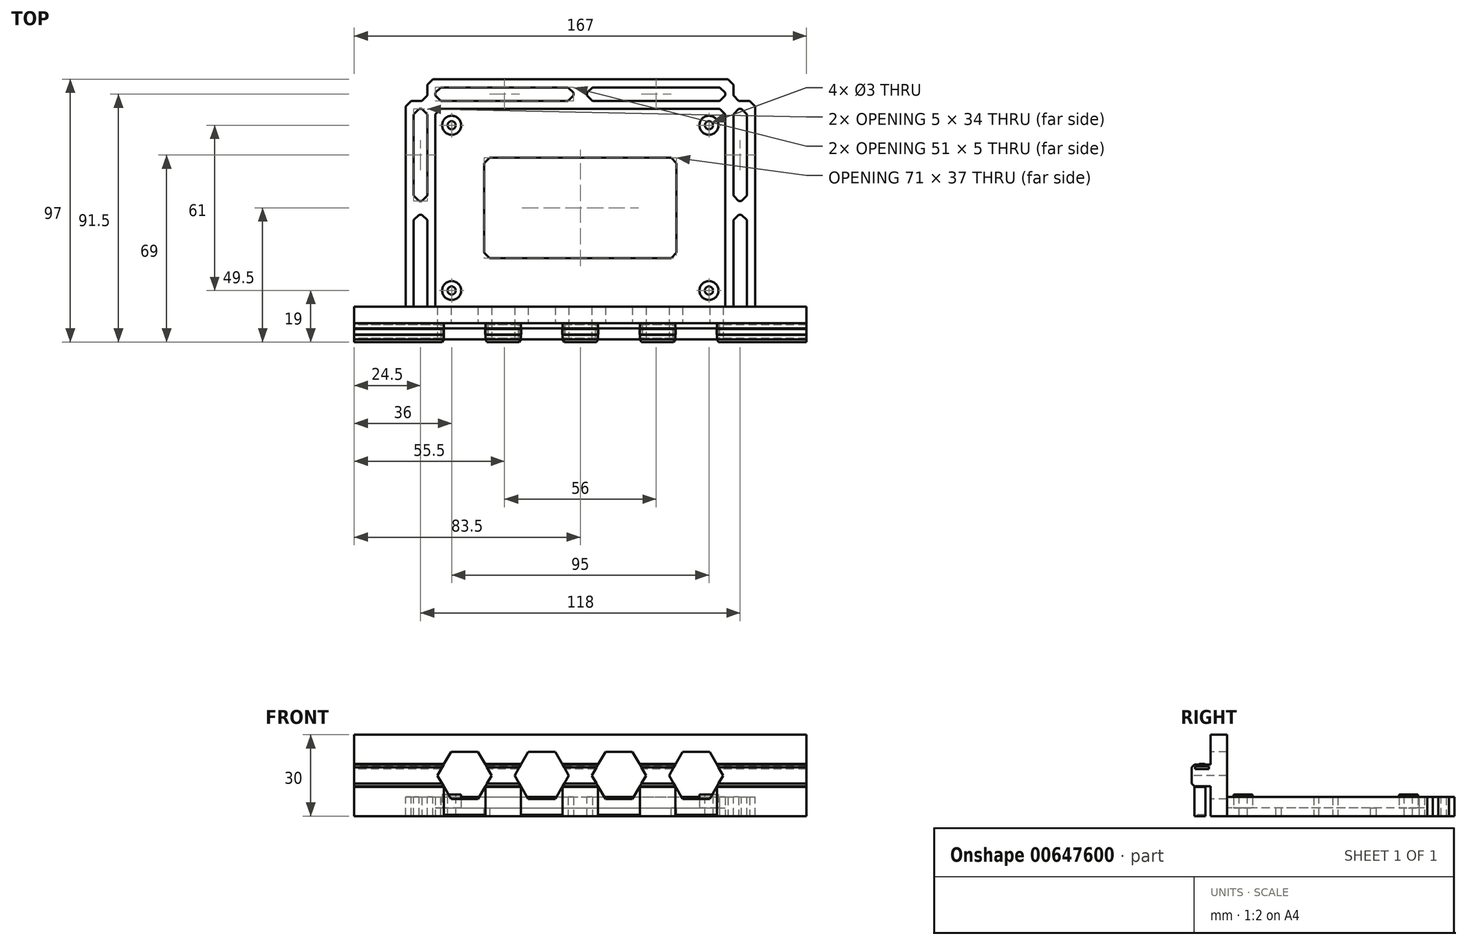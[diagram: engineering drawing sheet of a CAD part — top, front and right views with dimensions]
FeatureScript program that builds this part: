
annotation { "Feature Type Name" : "Feature", "Feature Type Description" : "" }
export const myFeature = defineFeature(function(context is Context, id is Id, definition is map)
    precondition{}
    {
        {
            var Q0;
            Q0=qCreatedBy(makeId("Top.planeOp"),FACE);
            var sketch = newSketch(context, id + "F0", { "sketchPlane" : qUnion([Q0])});
            skLineSegment(sketch, "E0.bottom", {"start": v(-47.5, 30.5) * mm, "end": v(47.5, 30.5) * mm, "construction": true});
            skLineSegment(sketch, "E0.top", {"start": v(-47.5, -30.5) * mm, "end": v(47.5, -30.5) * mm, "construction": true});
            skLineSegment(sketch, "E0.left", {"start": v(-47.5, 30.5) * mm, "end": v(-47.5, -30.5) * mm, "construction": true});
            skLineSegment(sketch, "E0.right", {"start": v(47.5, 30.5) * mm, "end": v(47.5, -30.5) * mm, "construction": true});
            skPoint(sketch, "E0.middle", {"position": v(0, 0) * mm});
            skCircle(sketch, "E1", {"center": v(-47.5, 30.5) * mm, "radius": 1.5 * mm});
            skCircle(sketch, "E2", {"center": v(47.5, 30.5) * mm, "radius": 1.5 * mm});
            skCircle(sketch, "E3", {"center": v(47.5, -30.5) * mm, "radius": 1.5 * mm});
            skCircle(sketch, "E4", {"center": v(-47.5, -30.5) * mm, "radius": 1.5 * mm});
            skCircle(sketch, "E5", {"center": v(-47.5, 30.5) * mm, "radius": 3.5 * mm});
            skCircle(sketch, "E6", {"center": v(47.5, 30.5) * mm, "radius": 3.5 * mm});
            skCircle(sketch, "E7", {"center": v(47.5, -30.5) * mm, "radius": 3.5 * mm});
            skCircle(sketch, "E8", {"center": v(-47.5, -30.5) * mm, "radius": 3.5 * mm});
            skLineSegment(sketch, "E9.0", {"start": v(-53.5, 44.5) * mm, "end": v(-53.5, -36.5) * mm});
            skLineSegment(sketch, "E9.1", {"start": v(-61.5, 36.5) * mm, "end": v(61.5, 36.5) * mm});
            skLineSegment(sketch, "E9.2", {"start": v(53.5, 44.5) * mm, "end": v(53.5, -36.5) * mm});
            skLineSegment(sketch, "E9.3", {"start": v(-83.5, -36.5) * mm, "end": v(83.5, -36.5) * mm});
            skLineSegment(sketch, "E10.0", {"start": v(-56.5, 47.5) * mm, "end": v(-56.5, -36.5) * mm});
            skLineSegment(sketch, "E10.1", {"start": v(-64.5, 39.5) * mm, "end": v(64.5, 39.5) * mm});
            skLineSegment(sketch, "E10.2", {"start": v(56.5, 47.5) * mm, "end": v(56.5, -36.5) * mm});
            skLineSegment(sketch, "E11.0", {"start": v(-61.5, 36.5) * mm, "end": v(-61.5, -36.5) * mm});
            skLineSegment(sketch, "E11.1", {"start": v(-53.5, 44.5) * mm, "end": v(53.5, 44.5) * mm});
            skLineSegment(sketch, "E11.2", {"start": v(61.5, 36.5) * mm, "end": v(61.5, -36.5) * mm});
            skLineSegment(sketch, "E12.0", {"start": v(-64.5, 39.5) * mm, "end": v(-64.5, -36.5) * mm});
            skLineSegment(sketch, "E12.1", {"start": v(-56.5, 47.5) * mm, "end": v(56.5, 47.5) * mm});
            skLineSegment(sketch, "E12.2", {"start": v(64.5, 39.5) * mm, "end": v(64.5, -36.5) * mm});
            skLineSegment(sketch, "E13.0", {"start": v(-35.5, 18.5) * mm, "end": v(-35.5, -18.5) * mm});
            skLineSegment(sketch, "E13.1", {"start": v(-35.5, 18.5) * mm, "end": v(35.5, 18.5) * mm});
            skLineSegment(sketch, "E13.2", {"start": v(35.5, 18.5) * mm, "end": v(35.5, -18.5) * mm});
            skLineSegment(sketch, "E13.3", {"start": v(-35.5, -18.5) * mm, "end": v(35.5, -18.5) * mm});
            skLineSegment(sketch, "E14", {"start": v(-83.5, -36.5) * mm, "end": v(-83.5, -42.5) * mm});
            skLineSegment(sketch, "E15", {"start": v(-83.5, -42.5) * mm, "end": v(83.5, -42.5) * mm});
            skLineSegment(sketch, "E16", {"start": v(83.5, -42.5) * mm, "end": v(83.5, -36.5) * mm});
            skPoint(sketch, "E17", {"position": v(0, -42.5) * mm});
            skLineSegment(sketch, "E18", {"start": v(-61.5, 2.5) * mm, "end": v(-56.5, 2.5) * mm});
            skLineSegment(sketch, "E19", {"start": v(-56.5, -2.5) * mm, "end": v(-61.5, -2.5) * mm});
            skLineSegment(sketch, "E20", {"start": v(-2.5, 44.5) * mm, "end": v(-2.5, 39.5) * mm});
            skLineSegment(sketch, "E21", {"start": v(2.5, 39.5) * mm, "end": v(2.5, 44.5) * mm});
            skLineSegment(sketch, "E22", {"start": v(56.5, 2.5) * mm, "end": v(61.5, 2.5) * mm});
            skLineSegment(sketch, "E23", {"start": v(61.5, -2.5) * mm, "end": v(56.5, -2.5) * mm});
            skPoint(sketch, "E24", {"position": v(0, 44.5) * mm});
            skPoint(sketch, "E25", {"position": v(-61.5, 0) * mm});
            skLineSegment(sketch, "E26", {"start": v(-61.5, 2.5) * mm, "end": v(-61.5, -2.5) * mm, "construction": true});
            skLineSegment(sketch, "E27", {"start": v(-2.5, 44.5) * mm, "end": v(2.5, 44.5) * mm, "construction": true});
            skSolve(sketch);
        }
        {
            var Q0;
            Q0=makeQuery(id+"F0.imprint","IMPRINT",FACE,{"disambiguationData":[TD([[makeQuery(id+"F0.imprint","IMPRINT",EDGE,{"derivedFrom":sQuery(id+"F0.wireOp",EDGE,"E5")}),-1.0]])]});
            var Q1;
            Q1=makeQuery(id+"F0.imprint","IMPRINT",FACE,{"disambiguationData":[TD([[makeQuery(id+"F0.imprint","IMPRINT",EDGE,{"derivedFrom":sQuery(id+"F0.wireOp",EDGE,"E1")}),-1.0]])]});
            var Q2;
            Q2=makeQuery(id+"F0.imprint","IMPRINT",FACE,{"disambiguationData":[TD([[makeQuery(id+"F0.imprint","IMPRINT",EDGE,{"derivedFrom":sQuery(id+"F0.wireOp",EDGE,"E4")}),-1.0]])]});
            var Q3;
            Q3=makeQuery(id+"F0.imprint","IMPRINT",FACE,{"disambiguationData":[TD([[makeQuery(id+"F0.imprint","IMPRINT",EDGE,{"derivedFrom":sQuery(id+"F0.wireOp",EDGE,"E3")}),-1.0]])]});
            var Q4;
            Q4=makeQuery(id+"F0.imprint","IMPRINT",FACE,{"disambiguationData":[TD([[makeQuery(id+"F0.imprint","IMPRINT",EDGE,{"derivedFrom":sQuery(id+"F0.wireOp",EDGE,"E2")}),-1.0]])]});
            var Q5;
            {var subQ0=sQuery(id+"F0.wireOp",EDGE,"E9.3");var subQ1=sQuery(id+"F0.wireOp",EDGE,"E9.0");var subQ2=makeQuery(id+"F0.imprint","INTERSECT",VERTEX,{"derivedFrom":[subQ1,subQ0]});Q5=makeQuery(id+"F0.imprint","IMPRINT",FACE,{"disambiguationData":[TD([[makeQuery(id+"F0.imprint","IMPRINT",EDGE,{"disambiguationData":[TD([[subQ2,1.0]])],"derivedFrom":subQ1}),-1.0]])]});}
            var Q6;
            {var subQ0=sQuery(id+"F0.wireOp",EDGE,"E12.0");Q6=makeQuery(id+"F0.imprint","IMPRINT",FACE,{"disambiguationData":[TD([[makeQuery(id+"F0.imprint","IMPRINT",EDGE,{"derivedFrom":subQ0}),1.0]])]});}
            var Q7;
            {var subQ0=sQuery(id+"F0.wireOp",EDGE,"E18");Q7=makeQuery(id+"F0.imprint","IMPRINT",FACE,{"disambiguationData":[TD([[makeQuery(id+"F0.imprint","IMPRINT",EDGE,{"derivedFrom":subQ0}),-1.0]])]});}
            var Q8;
            {var subQ0=sQuery(id+"F0.wireOp",EDGE,"E10.1");var subQ1=sQuery(id+"F0.wireOp",EDGE,"E9.0");var subQ2=makeQuery(id+"F0.imprint","INTERSECT",VERTEX,{"derivedFrom":[subQ1,subQ0]});Q8=makeQuery(id+"F0.imprint","IMPRINT",FACE,{"disambiguationData":[TD([[makeQuery(id+"F0.imprint","IMPRINT",EDGE,{"disambiguationData":[TD([[subQ2,-1.0]])],"derivedFrom":subQ1}),-1.0]])]});}
            var Q9;
            {var subQ13=sQuery(id+"F0.wireOp",EDGE,"E12.1");Q9=makeQuery(id+"F0.imprint","IMPRINT",FACE,{"disambiguationData":[TD([[makeQuery(id+"F0.imprint","IMPRINT",EDGE,{"derivedFrom":subQ13}),-1.0]])]});}
            var Q10;
            {var subQ0=sQuery(id+"F0.wireOp",EDGE,"E10.1");var subQ2=sQuery(id+"F0.wireOp",EDGE,"E9.0");var subQ3=makeQuery(id+"F0.imprint","INTERSECT",VERTEX,{"derivedFrom":[subQ2,subQ0]});Q10=makeQuery(id+"F0.imprint","IMPRINT",FACE,{"disambiguationData":[TD([[makeQuery(id+"F0.imprint","IMPRINT",EDGE,{"disambiguationData":[TD([[subQ3,-1.0]])],"derivedFrom":subQ2}),1.0]])]});}
            var Q11;
            {var subQ0=sQuery(id+"F0.wireOp",EDGE,"E14");Q11=makeQuery(id+"F0.imprint","IMPRINT",FACE,{"disambiguationData":[TD([[makeQuery(id+"F0.imprint","IMPRINT",EDGE,{"derivedFrom":subQ0}),1.0]])]});}
            var Q12;
            {var subQ0=sQuery(id+"F0.wireOp",EDGE,"E20");Q12=makeQuery(id+"F0.imprint","IMPRINT",FACE,{"disambiguationData":[TD([[makeQuery(id+"F0.imprint","IMPRINT",EDGE,{"derivedFrom":subQ0}),1.0]])]});}
            var Q13;
            {var subQ0=sQuery(id+"F0.wireOp",EDGE,"E9.2");var subQ1=sQuery(id+"F0.wireOp",EDGE,"E9.1");var subQ2=makeQuery(id+"F0.imprint","INTERSECT",VERTEX,{"derivedFrom":[subQ1,subQ0]});Q13=makeQuery(id+"F0.imprint","IMPRINT",FACE,{"disambiguationData":[TD([[makeQuery(id+"F0.imprint","IMPRINT",EDGE,{"disambiguationData":[TD([[subQ2,-1.0]])],"derivedFrom":subQ1}),1.0]])]});}
            var Q14;
            {var subQ0=sQuery(id+"F0.wireOp",EDGE,"E12.2");Q14=makeQuery(id+"F0.imprint","IMPRINT",FACE,{"disambiguationData":[TD([[makeQuery(id+"F0.imprint","IMPRINT",EDGE,{"derivedFrom":subQ0}),-1.0]])]});}
            var Q15;
            {var subQ0=sQuery(id+"F0.wireOp",EDGE,"E22");Q15=makeQuery(id+"F0.imprint","IMPRINT",FACE,{"disambiguationData":[TD([[makeQuery(id+"F0.imprint","IMPRINT",EDGE,{"derivedFrom":subQ0}),-1.0]])]});}
            var Q16;
            {var subQ2=sQuery(id+"F0.wireOp",EDGE,"E9.1");var subQ5=sQuery(id+"F0.wireOp",EDGE,"E9.2");var subQ7=makeQuery(id+"F0.imprint","INTERSECT",VERTEX,{"derivedFrom":[subQ2,subQ5]});Q16=makeQuery(id+"F0.imprint","IMPRINT",FACE,{"disambiguationData":[TD([[makeQuery(id+"F0.imprint","IMPRINT",EDGE,{"disambiguationData":[TD([[subQ7,-1.0]])],"derivedFrom":subQ2}),-1.0]])]});}
            extrude(context, id + "F1", {"entities" : qUnion([Q0, Q1, Q2, Q3, Q4, Q5, Q6, Q7, Q8, Q9, Q10, Q11, Q12, Q13, Q14, Q15, Q16]), "oppositeDirection" : true, "depth" : 3 * mm, "offsetDistance" : 25 * mm});
        }
        {
            var Q0;
            {var subQ0=sQuery(id+"F0.wireOp",EDGE,"E9.3");var subQ1=sQuery(id+"F0.wireOp",EDGE,"E9.0");var subQ2=makeQuery(id+"F0.imprint","INTERSECT",VERTEX,{"derivedFrom":[subQ1,subQ0]});Q0=makeQuery(id+"F0.imprint","IMPRINT",FACE,{"disambiguationData":[TD([[makeQuery(id+"F0.imprint","IMPRINT",EDGE,{"disambiguationData":[TD([[subQ2,1.0]])],"derivedFrom":subQ1}),-1.0]])]});}
            var Q1;
            {var subQ0=sQuery(id+"F0.wireOp",EDGE,"E10.1");var subQ1=sQuery(id+"F0.wireOp",EDGE,"E9.0");var subQ2=makeQuery(id+"F0.imprint","INTERSECT",VERTEX,{"derivedFrom":[subQ1,subQ0]});Q1=makeQuery(id+"F0.imprint","IMPRINT",FACE,{"disambiguationData":[TD([[makeQuery(id+"F0.imprint","IMPRINT",EDGE,{"disambiguationData":[TD([[subQ2,-1.0]])],"derivedFrom":subQ1}),-1.0]])]});}
            var Q2;
            {var subQ13=sQuery(id+"F0.wireOp",EDGE,"E12.1");Q2=makeQuery(id+"F0.imprint","IMPRINT",FACE,{"disambiguationData":[TD([[makeQuery(id+"F0.imprint","IMPRINT",EDGE,{"derivedFrom":subQ13}),-1.0]])]});}
            var Q3;
            {var subQ0=sQuery(id+"F0.wireOp",EDGE,"E12.0");Q3=makeQuery(id+"F0.imprint","IMPRINT",FACE,{"disambiguationData":[TD([[makeQuery(id+"F0.imprint","IMPRINT",EDGE,{"derivedFrom":subQ0}),1.0]])]});}
            var Q4;
            {var subQ0=sQuery(id+"F0.wireOp",EDGE,"E18");Q4=makeQuery(id+"F0.imprint","IMPRINT",FACE,{"disambiguationData":[TD([[makeQuery(id+"F0.imprint","IMPRINT",EDGE,{"derivedFrom":subQ0}),-1.0]])]});}
            var Q5;
            {var subQ0=sQuery(id+"F0.wireOp",EDGE,"E20");Q5=makeQuery(id+"F0.imprint","IMPRINT",FACE,{"disambiguationData":[TD([[makeQuery(id+"F0.imprint","IMPRINT",EDGE,{"derivedFrom":subQ0}),1.0]])]});}
            var Q6;
            {var subQ0=sQuery(id+"F0.wireOp",EDGE,"E10.1");var subQ2=sQuery(id+"F0.wireOp",EDGE,"E9.0");var subQ3=makeQuery(id+"F0.imprint","INTERSECT",VERTEX,{"derivedFrom":[subQ2,subQ0]});Q6=makeQuery(id+"F0.imprint","IMPRINT",FACE,{"disambiguationData":[TD([[makeQuery(id+"F0.imprint","IMPRINT",EDGE,{"disambiguationData":[TD([[subQ3,-1.0]])],"derivedFrom":subQ2}),1.0]])]});}
            var Q7;
            {var subQ0=sQuery(id+"F0.wireOp",EDGE,"E9.2");var subQ1=sQuery(id+"F0.wireOp",EDGE,"E9.1");var subQ2=makeQuery(id+"F0.imprint","INTERSECT",VERTEX,{"derivedFrom":[subQ1,subQ0]});Q7=makeQuery(id+"F0.imprint","IMPRINT",FACE,{"disambiguationData":[TD([[makeQuery(id+"F0.imprint","IMPRINT",EDGE,{"disambiguationData":[TD([[subQ2,-1.0]])],"derivedFrom":subQ1}),1.0]])]});}
            var Q8;
            {var subQ2=sQuery(id+"F0.wireOp",EDGE,"E9.1");var subQ5=sQuery(id+"F0.wireOp",EDGE,"E9.2");var subQ7=makeQuery(id+"F0.imprint","INTERSECT",VERTEX,{"derivedFrom":[subQ2,subQ5]});Q8=makeQuery(id+"F0.imprint","IMPRINT",FACE,{"disambiguationData":[TD([[makeQuery(id+"F0.imprint","IMPRINT",EDGE,{"disambiguationData":[TD([[subQ7,-1.0]])],"derivedFrom":subQ2}),-1.0]])]});}
            var Q9;
            {var subQ0=sQuery(id+"F0.wireOp",EDGE,"E12.2");Q9=makeQuery(id+"F0.imprint","IMPRINT",FACE,{"disambiguationData":[TD([[makeQuery(id+"F0.imprint","IMPRINT",EDGE,{"derivedFrom":subQ0}),-1.0]])]});}
            var Q10;
            {var subQ0=sQuery(id+"F0.wireOp",EDGE,"E22");Q10=makeQuery(id+"F0.imprint","IMPRINT",FACE,{"disambiguationData":[TD([[makeQuery(id+"F0.imprint","IMPRINT",EDGE,{"derivedFrom":subQ0}),-1.0]])]});}
            extrude(context, id + "F2", {"entities" : qUnion([Q0, Q1, Q2, Q3, Q4, Q5, Q6, Q7, Q8, Q9, Q10]), "operationType" : NewBodyOperationType.ADD, "depth" : 4 * mm, "offsetDistance" : 25 * mm});
        }
        {
            var Q0;
            Q0=makeQuery(id+"F0.imprint","IMPRINT",FACE,{"disambiguationData":[TD([[makeQuery(id+"F0.imprint","IMPRINT",EDGE,{"derivedFrom":sQuery(id+"F0.wireOp",EDGE,"E1")}),-1.0]])]});
            var Q1;
            Q1=makeQuery(id+"F0.imprint","IMPRINT",FACE,{"disambiguationData":[TD([[makeQuery(id+"F0.imprint","IMPRINT",EDGE,{"derivedFrom":sQuery(id+"F0.wireOp",EDGE,"E2")}),-1.0]])]});
            var Q2;
            Q2=makeQuery(id+"F0.imprint","IMPRINT",FACE,{"disambiguationData":[TD([[makeQuery(id+"F0.imprint","IMPRINT",EDGE,{"derivedFrom":sQuery(id+"F0.wireOp",EDGE,"E3")}),-1.0]])]});
            var Q3;
            Q3=makeQuery(id+"F0.imprint","IMPRINT",FACE,{"disambiguationData":[TD([[makeQuery(id+"F0.imprint","IMPRINT",EDGE,{"derivedFrom":sQuery(id+"F0.wireOp",EDGE,"E4")}),-1.0]])]});
            extrude(context, id + "F3", {"entities" : qUnion([Q0, Q1, Q2, Q3]), "operationType" : NewBodyOperationType.ADD, "depth" : 5 * mm, "offsetDistance" : 25 * mm});
        }
        {
            var Q0;
            {var subQ0=sQuery(id+"F0.wireOp",EDGE,"E14");Q0=makeQuery(id+"F0.imprint","IMPRINT",FACE,{"disambiguationData":[TD([[makeQuery(id+"F0.imprint","IMPRINT",EDGE,{"derivedFrom":subQ0}),1.0]])]});}
            extrude(context, id + "F4", {"entities" : qUnion([Q0]), "operationType" : NewBodyOperationType.ADD, "depth" : 27 * mm, "offsetDistance" : 25 * mm});
        }
        {
            var Q0;
            {var subQ0=sQuery(id+"F0.wireOp",EDGE,"E15");Q0=makeQuery(id+"F4.boolean.opBoolean","MERGE",FACE,{"derivedFrom":[makeQuery(id+"F1.opExtrude","SWEPT_FACE",FACE,{"disambiguationData":[OSD([subQ0])]}),makeQuery(id+"F4.opExtrude","SWEPT_FACE",FACE,{"disambiguationData":[OSD([subQ0])]})]});}
            var sketch = newSketch(context, id + "F5", { "sketchPlane" : qUnion([Q0])});
            skLineSegment(sketch, "E28.bottom", {"start": v(-83.5, 16) * mm, "end": v(83.5, 16) * mm});
            skLineSegment(sketch, "E28.top", {"start": v(-83.5, 8) * mm, "end": v(83.5, 8) * mm});
            skLineSegment(sketch, "E28.left", {"start": v(-83.5, 16) * mm, "end": v(-83.5, 8) * mm});
            skLineSegment(sketch, "E28.right", {"start": v(83.5, 16) * mm, "end": v(83.5, 8) * mm});
            skPoint(sketch, "E29", {"position": v(-83.5, 12) * mm});
            skCircle(sketch, "E30", {"center": v(-68.5, 12) * mm, "radius": 3.05 * mm});
            skCircle(sketch, "E31", {"center": v(-68.5, 12) * mm, "radius": 5.6 * mm});
            skCircle(sketch, "E32", {"center": v(68.5, 12) * mm, "radius": 3.05 * mm});
            skCircle(sketch, "E33", {"center": v(68.5, 12) * mm, "radius": 5.6 * mm});
            skCircle(sketch, "E34.cCircle", {"center": v(-42.75, 12) * mm, "radius": 10 * mm, "construction": true});
            skLineSegment(sketch, "E34.0", {"start": v(-32.75, 12) * mm, "end": v(-37.75, 3.34) * mm});
            skLineSegment(sketch, "E34.1", {"start": v(-37.75, 3.34) * mm, "end": v(-47.75, 3.34) * mm});
            skLineSegment(sketch, "E34.2", {"start": v(-47.75, 3.34) * mm, "end": v(-52.75, 12) * mm});
            skLineSegment(sketch, "E34.3", {"start": v(-52.75, 12) * mm, "end": v(-47.75, 20.66) * mm});
            skLineSegment(sketch, "E34.4", {"start": v(-47.75, 20.66) * mm, "end": v(-37.75, 20.66) * mm});
            skLineSegment(sketch, "E34.5", {"start": v(-37.75, 20.66) * mm, "end": v(-32.75, 12) * mm});
            skCircle(sketch, "E35.cCircle", {"center": v(-14.25, 12) * mm, "radius": 10 * mm, "construction": true});
            skLineSegment(sketch, "E35.0", {"start": v(-4.25, 12) * mm, "end": v(-9.25, 3.34) * mm});
            skLineSegment(sketch, "E35.1", {"start": v(-9.25, 3.34) * mm, "end": v(-19.25, 3.34) * mm});
            skLineSegment(sketch, "E35.2", {"start": v(-19.25, 3.34) * mm, "end": v(-24.25, 12) * mm});
            skLineSegment(sketch, "E35.3", {"start": v(-24.25, 12) * mm, "end": v(-19.25, 20.66) * mm});
            skLineSegment(sketch, "E35.4", {"start": v(-19.25, 20.66) * mm, "end": v(-9.25, 20.66) * mm});
            skLineSegment(sketch, "E35.5", {"start": v(-9.25, 20.66) * mm, "end": v(-4.25, 12) * mm});
            skCircle(sketch, "E36.cCircle", {"center": v(14.25, 12) * mm, "radius": 10 * mm, "construction": true});
            skLineSegment(sketch, "E36.0", {"start": v(24.25, 12) * mm, "end": v(19.25, 3.34) * mm});
            skLineSegment(sketch, "E36.1", {"start": v(19.25, 3.34) * mm, "end": v(9.25, 3.34) * mm});
            skLineSegment(sketch, "E36.2", {"start": v(9.25, 3.34) * mm, "end": v(4.25, 12) * mm});
            skLineSegment(sketch, "E36.3", {"start": v(4.25, 12) * mm, "end": v(9.25, 20.66) * mm});
            skLineSegment(sketch, "E36.4", {"start": v(9.25, 20.66) * mm, "end": v(19.25, 20.66) * mm});
            skLineSegment(sketch, "E36.5", {"start": v(19.25, 20.66) * mm, "end": v(24.25, 12) * mm});
            skCircle(sketch, "E37.cCircle", {"center": v(42.75, 12) * mm, "radius": 10 * mm, "construction": true});
            skLineSegment(sketch, "E37.0", {"start": v(52.75, 12) * mm, "end": v(47.75, 3.34) * mm});
            skLineSegment(sketch, "E37.1", {"start": v(47.75, 3.34) * mm, "end": v(37.75, 3.34) * mm});
            skLineSegment(sketch, "E37.2", {"start": v(37.75, 3.34) * mm, "end": v(32.75, 12) * mm});
            skLineSegment(sketch, "E37.3", {"start": v(32.75, 12) * mm, "end": v(37.75, 20.66) * mm});
            skLineSegment(sketch, "E37.4", {"start": v(37.75, 20.66) * mm, "end": v(47.75, 20.66) * mm});
            skLineSegment(sketch, "E37.5", {"start": v(47.75, 20.66) * mm, "end": v(52.75, 12) * mm});
            skLineSegment(sketch, "E38", {"start": v(-32.75, 12) * mm, "end": v(-24.25, 12) * mm, "construction": true});
            skLineSegment(sketch, "E39", {"start": v(-4.25, 12) * mm, "end": v(4.25, 12) * mm, "construction": true});
            skLineSegment(sketch, "E40", {"start": v(24.25, 12) * mm, "end": v(32.75, 12) * mm, "construction": true});
            skLineSegment(sketch, "E41", {"start": v(-68.5, 12) * mm, "end": v(-52.75, 12) * mm, "construction": true});
            skLineSegment(sketch, "E42", {"start": v(52.75, 12) * mm, "end": v(68.5, 12) * mm, "construction": true});
            skLineSegment(sketch, "E43", {"start": v(-83.5, 12) * mm, "end": v(-68.5, 12) * mm, "construction": true});
            skLineSegment(sketch, "E44", {"start": v(68.5, 12) * mm, "end": v(83.5, 12) * mm, "construction": true});
            skLineSegment(sketch, "E45", {"start": v(-76, 16) * mm, "end": v(-76, 8) * mm});
            skLineSegment(sketch, "E46", {"start": v(-61, 8) * mm, "end": v(-61, 16) * mm});
            skLineSegment(sketch, "E47", {"start": v(76, 16) * mm, "end": v(76, 8) * mm});
            skLineSegment(sketch, "E48", {"start": v(61, 8) * mm, "end": v(61, 16) * mm});
            skLineSegment(sketch, "E49", {"start": v(-76, 12) * mm, "end": v(-61, 12) * mm, "construction": true});
            skLineSegment(sketch, "E50", {"start": v(61, 12) * mm, "end": v(76, 12) * mm, "construction": true});
            skPoint(sketch, "E50.endSnap0", {"position": v(76, 12) * mm});
            skSolve(sketch);
        }
        {
            var Q0;
            {var subQ5=sQuery(id+"F5.wireOp",EDGE,"E34.4");Q0=makeQuery(id+"F5.imprint","IMPRINT",FACE,{"disambiguationData":[TD([[makeQuery(id+"F5.imprint","IMPRINT",EDGE,{"derivedFrom":subQ5}),-1.0]])]});}
            var Q1;
            {var subQ7=sQuery(id+"F5.wireOp",EDGE,"E28.bottom");var subQ9=sQuery(id+"F5.wireOp",EDGE,"E34.3");var subQ11=makeQuery(id+"F5.imprint","INTERSECT",VERTEX,{"derivedFrom":[subQ7,subQ9]});Q1=makeQuery(id+"F5.imprint","IMPRINT",FACE,{"disambiguationData":[TD([[makeQuery(id+"F5.imprint","IMPRINT",EDGE,{"disambiguationData":[TD([[subQ11,-1.0]])],"derivedFrom":subQ7}),-1.0]])]});}
            var Q2;
            {var subQ5=sQuery(id+"F5.wireOp",EDGE,"E34.1");Q2=makeQuery(id+"F5.imprint","IMPRINT",FACE,{"disambiguationData":[TD([[makeQuery(id+"F5.imprint","IMPRINT",EDGE,{"derivedFrom":subQ5}),-1.0]])]});}
            var Q3;
            {var subQ5=sQuery(id+"F5.wireOp",EDGE,"E35.1");Q3=makeQuery(id+"F5.imprint","IMPRINT",FACE,{"disambiguationData":[TD([[makeQuery(id+"F5.imprint","IMPRINT",EDGE,{"derivedFrom":subQ5}),-1.0]])]});}
            var Q4;
            {var subQ0=sQuery(id+"F5.wireOp",EDGE,"E35.3");var subQ9=sQuery(id+"F5.wireOp",EDGE,"E28.bottom");var subQ10=makeQuery(id+"F5.imprint","INTERSECT",VERTEX,{"derivedFrom":[subQ9,subQ0]});Q4=makeQuery(id+"F5.imprint","IMPRINT",FACE,{"disambiguationData":[TD([[makeQuery(id+"F5.imprint","IMPRINT",EDGE,{"disambiguationData":[TD([[subQ10,-1.0]])],"derivedFrom":subQ9}),-1.0]])]});}
            var Q5;
            {var subQ5=sQuery(id+"F5.wireOp",EDGE,"E35.4");Q5=makeQuery(id+"F5.imprint","IMPRINT",FACE,{"disambiguationData":[TD([[makeQuery(id+"F5.imprint","IMPRINT",EDGE,{"derivedFrom":subQ5}),-1.0]])]});}
            var Q6;
            {var subQ5=sQuery(id+"F5.wireOp",EDGE,"E36.4");Q6=makeQuery(id+"F5.imprint","IMPRINT",FACE,{"disambiguationData":[TD([[makeQuery(id+"F5.imprint","IMPRINT",EDGE,{"derivedFrom":subQ5}),-1.0]])]});}
            var Q7;
            {var subQ0=sQuery(id+"F5.wireOp",EDGE,"E36.3");var subQ9=sQuery(id+"F5.wireOp",EDGE,"E28.bottom");var subQ10=makeQuery(id+"F5.imprint","INTERSECT",VERTEX,{"derivedFrom":[subQ9,subQ0]});Q7=makeQuery(id+"F5.imprint","IMPRINT",FACE,{"disambiguationData":[TD([[makeQuery(id+"F5.imprint","IMPRINT",EDGE,{"disambiguationData":[TD([[subQ10,-1.0]])],"derivedFrom":subQ9}),-1.0]])]});}
            var Q8;
            {var subQ5=sQuery(id+"F5.wireOp",EDGE,"E36.1");Q8=makeQuery(id+"F5.imprint","IMPRINT",FACE,{"disambiguationData":[TD([[makeQuery(id+"F5.imprint","IMPRINT",EDGE,{"derivedFrom":subQ5}),-1.0]])]});}
            var Q9;
            {var subQ5=sQuery(id+"F5.wireOp",EDGE,"E37.1");Q9=makeQuery(id+"F5.imprint","IMPRINT",FACE,{"disambiguationData":[TD([[makeQuery(id+"F5.imprint","IMPRINT",EDGE,{"derivedFrom":subQ5}),-1.0]])]});}
            var Q10;
            {var subQ0=sQuery(id+"F5.wireOp",EDGE,"E37.3");var subQ9=sQuery(id+"F5.wireOp",EDGE,"E28.bottom");var subQ10=makeQuery(id+"F5.imprint","INTERSECT",VERTEX,{"derivedFrom":[subQ9,subQ0]});Q10=makeQuery(id+"F5.imprint","IMPRINT",FACE,{"disambiguationData":[TD([[makeQuery(id+"F5.imprint","IMPRINT",EDGE,{"disambiguationData":[TD([[subQ10,-1.0]])],"derivedFrom":subQ9}),-1.0]])]});}
            var Q11;
            {var subQ5=sQuery(id+"F5.wireOp",EDGE,"E37.4");Q11=makeQuery(id+"F5.imprint","IMPRINT",FACE,{"disambiguationData":[TD([[makeQuery(id+"F5.imprint","IMPRINT",EDGE,{"derivedFrom":subQ5}),-1.0]])]});}
            var Q12;
            {var subQ0=sQuery(id+"F0.wireOp",EDGE,"E9.3");Q12=makeQuery(id+"F4.boolean.opBoolean","MERGE",FACE,{"derivedFrom":[makeQuery(id+"F1.opExtrude","SWEPT_FACE",FACE,{"disambiguationData":[OSD([subQ0]),TDD([makeQuery(id+"F0.imprint","IMPRINT",EDGE,{"disambiguationData":[TD([[makeQuery(id+"F0.imprint","INTERSECT",VERTEX,{"derivedFrom":[subQ0,sQuery(id+"F0.wireOp",EDGE,"E14")]}),-1.0]])],"derivedFrom":subQ0})])]}),makeQuery(id+"F1.opExtrude","SWEPT_FACE",FACE,{"disambiguationData":[OSD([subQ0]),TDD([makeQuery(id+"F0.imprint","IMPRINT",EDGE,{"disambiguationData":[TD([[makeQuery(id+"F0.imprint","INTERSECT",VERTEX,{"derivedFrom":[subQ0,sQuery(id+"F0.wireOp",EDGE,"E10.0")]}),1.0]])],"derivedFrom":subQ0})])]}),makeQuery(id+"F1.opExtrude","SWEPT_FACE",FACE,{"disambiguationData":[OSD([subQ0]),TDD([makeQuery(id+"F0.imprint","IMPRINT",EDGE,{"disambiguationData":[TD([[makeQuery(id+"F0.imprint","INTERSECT",VERTEX,{"derivedFrom":[subQ0,sQuery(id+"F0.wireOp",EDGE,"E10.2")]}),-1.0]])],"derivedFrom":subQ0})])]}),makeQuery(id+"F1.opExtrude","SWEPT_FACE",FACE,{"disambiguationData":[OSD([subQ0]),TDD([makeQuery(id+"F0.imprint","IMPRINT",EDGE,{"disambiguationData":[TD([[makeQuery(id+"F0.imprint","INTERSECT",VERTEX,{"derivedFrom":[subQ0,sQuery(id+"F0.wireOp",EDGE,"E16")]}),1.0]])],"derivedFrom":subQ0})])]}),makeQuery(id+"F4.opExtrude","SWEPT_FACE",FACE,{"disambiguationData":[OSD([subQ0])]})]});}
            extrude(context, id + "F6", {"entities" : qUnion([Q0, Q1, Q2, Q3, Q4, Q5, Q6, Q7, Q8, Q9, Q10, Q11]), "operationType" : NewBodyOperationType.REMOVE, "endBound" : BoundingType.UP_TO_SURFACE, "oppositeDirection" : true, "depth" : 25 * mm, "endBoundEntityFace" : qUnion([Q12]), "offsetDistance" : 25 * mm});
        }
        {
            var Q0;
            {var subQ0=sQuery(id+"F5.wireOp",EDGE,"E28.left");Q0=makeQuery(id+"F5.imprint","IMPRINT",FACE,{"disambiguationData":[TD([[makeQuery(id+"F5.imprint","IMPRINT",EDGE,{"derivedFrom":subQ0}),-1.0]])]});}
            var Q1;
            {var subQ0=sQuery(id+"F5.wireOp",EDGE,"E28.right");Q1=makeQuery(id+"F5.imprint","IMPRINT",FACE,{"disambiguationData":[TD([[makeQuery(id+"F5.imprint","IMPRINT",EDGE,{"derivedFrom":subQ0}),1.0]])]});}
            var Q2;
            {var subQ7=sQuery(id+"F5.wireOp",EDGE,"E48");Q2=makeQuery(id+"F5.imprint","IMPRINT",FACE,{"disambiguationData":[TD([[makeQuery(id+"F5.imprint","IMPRINT",EDGE,{"derivedFrom":subQ7}),1.0]])]});}
            var Q3;
            {var subQ0=sQuery(id+"F5.wireOp",EDGE,"E36.5");var subQ7=sQuery(id+"F5.wireOp",EDGE,"E28.bottom");var subQ8=makeQuery(id+"F5.imprint","INTERSECT",VERTEX,{"derivedFrom":[subQ7,subQ0]});Q3=makeQuery(id+"F5.imprint","IMPRINT",FACE,{"disambiguationData":[TD([[makeQuery(id+"F5.imprint","IMPRINT",EDGE,{"disambiguationData":[TD([[subQ8,-1.0]])],"derivedFrom":subQ7}),-1.0]])]});}
            var Q4;
            {var subQ0=sQuery(id+"F5.wireOp",EDGE,"E35.5");var subQ5=sQuery(id+"F5.wireOp",EDGE,"E28.bottom");var subQ6=makeQuery(id+"F5.imprint","INTERSECT",VERTEX,{"derivedFrom":[subQ5,subQ0]});Q4=makeQuery(id+"F5.imprint","IMPRINT",FACE,{"disambiguationData":[TD([[makeQuery(id+"F5.imprint","IMPRINT",EDGE,{"disambiguationData":[TD([[subQ6,-1.0]])],"derivedFrom":subQ5}),-1.0]])]});}
            var Q5;
            {var subQ0=sQuery(id+"F5.wireOp",EDGE,"E34.5");var subQ3=sQuery(id+"F5.wireOp",EDGE,"E28.bottom");var subQ4=makeQuery(id+"F5.imprint","INTERSECT",VERTEX,{"derivedFrom":[subQ3,subQ0]});Q5=makeQuery(id+"F5.imprint","IMPRINT",FACE,{"disambiguationData":[TD([[makeQuery(id+"F5.imprint","IMPRINT",EDGE,{"disambiguationData":[TD([[subQ4,-1.0]])],"derivedFrom":subQ3}),-1.0]])]});}
            var Q6;
            {var subQ7=sQuery(id+"F5.wireOp",EDGE,"E46");Q6=makeQuery(id+"F5.imprint","IMPRINT",FACE,{"disambiguationData":[TD([[makeQuery(id+"F5.imprint","IMPRINT",EDGE,{"derivedFrom":subQ7}),-1.0]])]});}
            var Q7;
            {var subQ0=sQuery(id+"F5.wireOp",EDGE,"E48");Q7=makeQuery(id+"F5.imprint","IMPRINT",FACE,{"disambiguationData":[TD([[makeQuery(id+"F5.imprint","IMPRINT",EDGE,{"derivedFrom":subQ0}),-1.0]])]});}
            var Q8;
            Q8=makeQuery(id+"F5.imprint","IMPRINT",FACE,{"disambiguationData":[TD([[makeQuery(id+"F5.imprint","IMPRINT",EDGE,{"derivedFrom":sQuery(id+"F5.wireOp",EDGE,"E32")}),-1.0]])]});
            var Q9;
            Q9=makeQuery(id+"F5.imprint","IMPRINT",FACE,{"disambiguationData":[TD([[makeQuery(id+"F5.imprint","IMPRINT",EDGE,{"derivedFrom":sQuery(id+"F5.wireOp",EDGE,"E32")}),1.0]])]});
            var Q10;
            {var subQ0=sQuery(id+"F5.wireOp",EDGE,"E47");Q10=makeQuery(id+"F5.imprint","IMPRINT",FACE,{"disambiguationData":[TD([[makeQuery(id+"F5.imprint","IMPRINT",EDGE,{"derivedFrom":subQ0}),-1.0]])]});}
            var Q11;
            {var subQ0=sQuery(id+"F5.wireOp",EDGE,"E46");Q11=makeQuery(id+"F5.imprint","IMPRINT",FACE,{"disambiguationData":[TD([[makeQuery(id+"F5.imprint","IMPRINT",EDGE,{"derivedFrom":subQ0}),1.0]])]});}
            var Q12;
            Q12=makeQuery(id+"F5.imprint","IMPRINT",FACE,{"disambiguationData":[TD([[makeQuery(id+"F5.imprint","IMPRINT",EDGE,{"derivedFrom":sQuery(id+"F5.wireOp",EDGE,"E30")}),-1.0]])]});
            var Q13;
            Q13=makeQuery(id+"F5.imprint","IMPRINT",FACE,{"disambiguationData":[TD([[makeQuery(id+"F5.imprint","IMPRINT",EDGE,{"derivedFrom":sQuery(id+"F5.wireOp",EDGE,"E30")}),1.0]])]});
            var Q14;
            {var subQ0=sQuery(id+"F5.wireOp",EDGE,"E45");Q14=makeQuery(id+"F5.imprint","IMPRINT",FACE,{"disambiguationData":[TD([[makeQuery(id+"F5.imprint","IMPRINT",EDGE,{"derivedFrom":subQ0}),1.0]])]});}
            extrude(context, id + "F7", {"entities" : qUnion([Q0, Q1, Q2, Q3, Q4, Q5, Q6, Q7, Q8, Q9, Q10, Q11, Q12, Q13, Q14]), "operationType" : NewBodyOperationType.ADD, "depth" : 7 * mm, "offsetDistance" : 25 * mm});
        }
        {
            var Q0;
            {var subQ0=sQuery(id+"F5.wireOp",EDGE,"E28.top");Q0=makeQuery(id+"F7.opExtrude","CAP_EDGE",EDGE,{"disambiguationData":[OSD([subQ0]),TDD([makeQuery(id+"F5.imprint","IMPRINT",EDGE,{"disambiguationData":[TD([[makeQuery(id+"F5.imprint","INTERSECT",VERTEX,{"derivedFrom":[subQ0,sQuery(id+"F5.wireOp",EDGE,"E45")]}),1.0]])],"derivedFrom":subQ0})])],"isStart":false});}
            var Q1;
            {var subQ0=sQuery(id+"F5.wireOp",EDGE,"E28.bottom");Q1=makeQuery(id+"F7.opExtrude","CAP_EDGE",EDGE,{"disambiguationData":[OSD([subQ0]),TDD([makeQuery(id+"F5.imprint","IMPRINT",EDGE,{"disambiguationData":[TD([[makeQuery(id+"F5.imprint","INTERSECT",VERTEX,{"derivedFrom":[subQ0,sQuery(id+"F5.wireOp",EDGE,"E45")]}),1.0]])],"derivedFrom":subQ0})])],"isStart":false});}
            var Q2;
            {var subQ0=sQuery(id+"F5.wireOp",EDGE,"E28.bottom");var subQ1=sQuery(id+"F5.wireOp",EDGE,"E31");var subQ3=makeQuery(id+"F5.imprint","INTERSECT",VERTEX,{"disambiguationData":[OD(0.0)],"derivedFrom":[subQ0,subQ1]});Q2=makeQuery(id+"FDtMRLwZ7YmErVr_1.opExtrude","CAP_EDGE",EDGE,{"disambiguationData":[OSD([subQ0]),TDD([makeQuery(id+"F5.imprint","IMPRINT",EDGE,{"disambiguationData":[TD([[makeQuery(id+"F5.imprint","INTERSECT",VERTEX,{"derivedFrom":[subQ0,sQuery(id+"F5.wireOp",EDGE,"E45")]}),-1.0]])],"derivedFrom":subQ0}),makeQuery(id+"F5.imprint","IMPRINT",EDGE,{"disambiguationData":[TD([[subQ3,-1.0]])],"derivedFrom":subQ0}),makeQuery(id+"F5.imprint","IMPRINT",EDGE,{"disambiguationData":[TD([[makeQuery(id+"F5.imprint","INTERSECT",VERTEX,{"derivedFrom":[subQ0,sQuery(id+"F5.wireOp",EDGE,"E46")]}),1.0]])],"derivedFrom":subQ0})])],"isStart":false});}
            var Q3;
            {var subQ0=sQuery(id+"F5.wireOp",EDGE,"E28.top");var subQ1=sQuery(id+"F5.wireOp",EDGE,"E31");var subQ3=makeQuery(id+"F5.imprint","INTERSECT",VERTEX,{"disambiguationData":[OD(0.0)],"derivedFrom":[subQ0,subQ1]});Q3=makeQuery(id+"FDtMRLwZ7YmErVr_1.opExtrude","CAP_EDGE",EDGE,{"disambiguationData":[OSD([subQ0]),TDD([makeQuery(id+"F5.imprint","IMPRINT",EDGE,{"disambiguationData":[TD([[makeQuery(id+"F5.imprint","INTERSECT",VERTEX,{"derivedFrom":[subQ0,sQuery(id+"F5.wireOp",EDGE,"E45")]}),-1.0]])],"derivedFrom":subQ0}),makeQuery(id+"F5.imprint","IMPRINT",EDGE,{"disambiguationData":[TD([[subQ3,-1.0]])],"derivedFrom":subQ0}),makeQuery(id+"F5.imprint","IMPRINT",EDGE,{"disambiguationData":[TD([[makeQuery(id+"F5.imprint","INTERSECT",VERTEX,{"derivedFrom":[subQ0,sQuery(id+"F5.wireOp",EDGE,"E46")]}),1.0]])],"derivedFrom":subQ0})])],"isStart":false});}
            var Q4;
            {var subQ0=sQuery(id+"F5.wireOp",EDGE,"E28.top");Q4=makeQuery(id+"F7.opExtrude","CAP_EDGE",EDGE,{"disambiguationData":[OSD([subQ0]),TDD([makeQuery(id+"F5.imprint","IMPRINT",EDGE,{"disambiguationData":[TD([[makeQuery(id+"F5.imprint","INTERSECT",VERTEX,{"derivedFrom":[subQ0,sQuery(id+"F5.wireOp",EDGE,"E46")]}),-1.0]])],"derivedFrom":subQ0})])],"isStart":false});}
            var Q5;
            {var subQ0=sQuery(id+"F5.wireOp",EDGE,"E28.bottom");Q5=makeQuery(id+"F7.opExtrude","CAP_EDGE",EDGE,{"disambiguationData":[OSD([subQ0]),TDD([makeQuery(id+"F5.imprint","IMPRINT",EDGE,{"disambiguationData":[TD([[makeQuery(id+"F5.imprint","INTERSECT",VERTEX,{"derivedFrom":[subQ0,sQuery(id+"F5.wireOp",EDGE,"E46")]}),-1.0]])],"derivedFrom":subQ0})])],"isStart":false});}
            var Q6;
            {var subQ0=sQuery(id+"F5.wireOp",EDGE,"E28.bottom");Q6=makeQuery(id+"F7.opExtrude","CAP_EDGE",EDGE,{"disambiguationData":[OSD([subQ0]),TDD([makeQuery(id+"F5.imprint","IMPRINT",EDGE,{"disambiguationData":[TD([[makeQuery(id+"F5.imprint","INTERSECT",VERTEX,{"derivedFrom":[subQ0,sQuery(id+"F5.wireOp",EDGE,"E34.5")]}),-1.0]])],"derivedFrom":subQ0})])],"isStart":false});}
            var Q7;
            {var subQ0=sQuery(id+"F5.wireOp",EDGE,"E28.top");Q7=makeQuery(id+"F7.opExtrude","CAP_EDGE",EDGE,{"disambiguationData":[OSD([subQ0]),TDD([makeQuery(id+"F5.imprint","IMPRINT",EDGE,{"disambiguationData":[TD([[makeQuery(id+"F5.imprint","INTERSECT",VERTEX,{"derivedFrom":[subQ0,sQuery(id+"F5.wireOp",EDGE,"E34.0")]}),-1.0]])],"derivedFrom":subQ0})])],"isStart":false});}
            var Q8;
            {var subQ0=sQuery(id+"F5.wireOp",EDGE,"E28.top");Q8=makeQuery(id+"F7.opExtrude","CAP_EDGE",EDGE,{"disambiguationData":[OSD([subQ0]),TDD([makeQuery(id+"F5.imprint","IMPRINT",EDGE,{"disambiguationData":[TD([[makeQuery(id+"F5.imprint","INTERSECT",VERTEX,{"derivedFrom":[subQ0,sQuery(id+"F5.wireOp",EDGE,"E35.0")]}),-1.0]])],"derivedFrom":subQ0})])],"isStart":false});}
            var Q9;
            {var subQ0=sQuery(id+"F5.wireOp",EDGE,"E28.bottom");Q9=makeQuery(id+"F7.opExtrude","CAP_EDGE",EDGE,{"disambiguationData":[OSD([subQ0]),TDD([makeQuery(id+"F5.imprint","IMPRINT",EDGE,{"disambiguationData":[TD([[makeQuery(id+"F5.imprint","INTERSECT",VERTEX,{"derivedFrom":[subQ0,sQuery(id+"F5.wireOp",EDGE,"E35.5")]}),-1.0]])],"derivedFrom":subQ0})])],"isStart":false});}
            var Q10;
            {var subQ0=sQuery(id+"F5.wireOp",EDGE,"E28.bottom");Q10=makeQuery(id+"F7.opExtrude","CAP_EDGE",EDGE,{"disambiguationData":[OSD([subQ0]),TDD([makeQuery(id+"F5.imprint","IMPRINT",EDGE,{"disambiguationData":[TD([[makeQuery(id+"F5.imprint","INTERSECT",VERTEX,{"derivedFrom":[subQ0,sQuery(id+"F5.wireOp",EDGE,"E36.5")]}),-1.0]])],"derivedFrom":subQ0})])],"isStart":false});}
            var Q11;
            {var subQ0=sQuery(id+"F5.wireOp",EDGE,"E28.top");Q11=makeQuery(id+"F7.opExtrude","CAP_EDGE",EDGE,{"disambiguationData":[OSD([subQ0]),TDD([makeQuery(id+"F5.imprint","IMPRINT",EDGE,{"disambiguationData":[TD([[makeQuery(id+"F5.imprint","INTERSECT",VERTEX,{"derivedFrom":[subQ0,sQuery(id+"F5.wireOp",EDGE,"E36.0")]}),-1.0]])],"derivedFrom":subQ0})])],"isStart":false});}
            var Q12;
            {var subQ0=sQuery(id+"F5.wireOp",EDGE,"E28.top");Q12=makeQuery(id+"F7.opExtrude","CAP_EDGE",EDGE,{"disambiguationData":[OSD([subQ0]),TDD([makeQuery(id+"F5.imprint","IMPRINT",EDGE,{"disambiguationData":[TD([[makeQuery(id+"F5.imprint","INTERSECT",VERTEX,{"derivedFrom":[subQ0,sQuery(id+"F5.wireOp",EDGE,"E48")]}),1.0]])],"derivedFrom":subQ0})])],"isStart":false});}
            var Q13;
            {var subQ0=sQuery(id+"F5.wireOp",EDGE,"E28.bottom");Q13=makeQuery(id+"F7.opExtrude","CAP_EDGE",EDGE,{"disambiguationData":[OSD([subQ0]),TDD([makeQuery(id+"F5.imprint","IMPRINT",EDGE,{"disambiguationData":[TD([[makeQuery(id+"F5.imprint","INTERSECT",VERTEX,{"derivedFrom":[subQ0,sQuery(id+"F5.wireOp",EDGE,"E48")]}),1.0]])],"derivedFrom":subQ0})])],"isStart":false});}
            var Q14;
            {var subQ0=sQuery(id+"F5.wireOp",EDGE,"E28.bottom");var subQ1=sQuery(id+"F5.wireOp",EDGE,"E33");var subQ3=makeQuery(id+"F5.imprint","INTERSECT",VERTEX,{"disambiguationData":[OD(0.0)],"derivedFrom":[subQ0,subQ1]});Q14=makeQuery(id+"FDtMRLwZ7YmErVr_1.opExtrude","CAP_EDGE",EDGE,{"disambiguationData":[OSD([subQ0]),TDD([makeQuery(id+"F5.imprint","IMPRINT",EDGE,{"disambiguationData":[TD([[makeQuery(id+"F5.imprint","INTERSECT",VERTEX,{"derivedFrom":[subQ0,sQuery(id+"F5.wireOp",EDGE,"E48")]}),-1.0]])],"derivedFrom":subQ0}),makeQuery(id+"F5.imprint","IMPRINT",EDGE,{"disambiguationData":[TD([[subQ3,-1.0]])],"derivedFrom":subQ0}),makeQuery(id+"F5.imprint","IMPRINT",EDGE,{"disambiguationData":[TD([[makeQuery(id+"F5.imprint","INTERSECT",VERTEX,{"derivedFrom":[subQ0,sQuery(id+"F5.wireOp",EDGE,"E47")]}),1.0]])],"derivedFrom":subQ0})])],"isStart":false});}
            var Q15;
            {var subQ0=sQuery(id+"F5.wireOp",EDGE,"E28.top");var subQ1=sQuery(id+"F5.wireOp",EDGE,"E33");var subQ3=makeQuery(id+"F5.imprint","INTERSECT",VERTEX,{"disambiguationData":[OD(0.0)],"derivedFrom":[subQ0,subQ1]});Q15=makeQuery(id+"FDtMRLwZ7YmErVr_1.opExtrude","CAP_EDGE",EDGE,{"disambiguationData":[OSD([subQ0]),TDD([makeQuery(id+"F5.imprint","IMPRINT",EDGE,{"disambiguationData":[TD([[makeQuery(id+"F5.imprint","INTERSECT",VERTEX,{"derivedFrom":[subQ0,sQuery(id+"F5.wireOp",EDGE,"E48")]}),-1.0]])],"derivedFrom":subQ0}),makeQuery(id+"F5.imprint","IMPRINT",EDGE,{"disambiguationData":[TD([[subQ3,-1.0]])],"derivedFrom":subQ0}),makeQuery(id+"F5.imprint","IMPRINT",EDGE,{"disambiguationData":[TD([[makeQuery(id+"F5.imprint","INTERSECT",VERTEX,{"derivedFrom":[subQ0,sQuery(id+"F5.wireOp",EDGE,"E47")]}),1.0]])],"derivedFrom":subQ0})])],"isStart":false});}
            var Q16;
            {var subQ0=sQuery(id+"F5.wireOp",EDGE,"E28.top");Q16=makeQuery(id+"F7.opExtrude","CAP_EDGE",EDGE,{"disambiguationData":[OSD([subQ0]),TDD([makeQuery(id+"F5.imprint","IMPRINT",EDGE,{"disambiguationData":[TD([[makeQuery(id+"F5.imprint","INTERSECT",VERTEX,{"derivedFrom":[subQ0,sQuery(id+"F5.wireOp",EDGE,"E47")]}),-1.0]])],"derivedFrom":subQ0})])],"isStart":false});}
            var Q17;
            {var subQ0=sQuery(id+"F5.wireOp",EDGE,"E28.bottom");Q17=makeQuery(id+"F7.opExtrude","CAP_EDGE",EDGE,{"disambiguationData":[OSD([subQ0]),TDD([makeQuery(id+"F5.imprint","IMPRINT",EDGE,{"disambiguationData":[TD([[makeQuery(id+"F5.imprint","INTERSECT",VERTEX,{"derivedFrom":[subQ0,sQuery(id+"F5.wireOp",EDGE,"E47")]}),-1.0]])],"derivedFrom":subQ0})])],"isStart":false});}
            var Q18;
            Q18=makeQuery(id+"F7.opExtrude","CAP_EDGE",EDGE,{"disambiguationData":[OSD([sQuery(id+"F5.wireOp",EDGE,"E45")])],"isStart":false});
            var Q19;
            Q19=makeQuery(id+"F7.opExtrude","CAP_EDGE",EDGE,{"disambiguationData":[OSD([sQuery(id+"F5.wireOp",EDGE,"E46")])],"isStart":false});
            var Q20;
            Q20=makeQuery(id+"F7.opExtrude","CAP_EDGE",EDGE,{"disambiguationData":[OSD([sQuery(id+"F5.wireOp",EDGE,"E48")])],"isStart":false});
            var Q21;
            Q21=makeQuery(id+"F7.opExtrude","CAP_EDGE",EDGE,{"disambiguationData":[OSD([sQuery(id+"F5.wireOp",EDGE,"E47")])],"isStart":false});
            chamfer(context, id + "F8", {"entities" : qUnion([Q0, Q1, Q2, Q3, Q4, Q5, Q6, Q7, Q8, Q9, Q10, Q11, Q12, Q13, Q14, Q15, Q16, Q17, Q18, Q19, Q20, Q21]), "width" : 1 * mm});
        }
        {
            var Q0;
            Q0=makeQuery(id+"F1.opExtrude","SWEPT_EDGE",EDGE,{"disambiguationData":[OSD([sQuery(id+"F0.wireOp",EDGE,"E13.1"),sQuery(id+"F0.wireOp",EDGE,"E13.2")])]});
            var Q1;
            Q1=makeQuery(id+"F1.opExtrude","SWEPT_EDGE",EDGE,{"disambiguationData":[OSD([sQuery(id+"F0.wireOp",EDGE,"E13.2"),sQuery(id+"F0.wireOp",EDGE,"E13.3")])]});
            var Q2;
            Q2=makeQuery(id+"F1.opExtrude","SWEPT_EDGE",EDGE,{"disambiguationData":[OSD([sQuery(id+"F0.wireOp",EDGE,"E13.0"),sQuery(id+"F0.wireOp",EDGE,"E13.1")])]});
            var Q3;
            Q3=makeQuery(id+"F1.opExtrude","SWEPT_EDGE",EDGE,{"disambiguationData":[OSD([sQuery(id+"F0.wireOp",EDGE,"E13.0"),sQuery(id+"F0.wireOp",EDGE,"E13.3")])]});
            var Q4;
            Q4=makeQuery(id+"F2.opExtrude","SWEPT_EDGE",EDGE,{"disambiguationData":[OSD([sQuery(id+"F0.wireOp",EDGE,"E9.2"),sQuery(id+"F0.wireOp",EDGE,"E9.3")])]});
            var Q5;
            {var subQ0=sQuery(id+"F0.wireOp",EDGE,"E11.2");var subQ1=sQuery(id+"F0.wireOp",EDGE,"E9.3");Q5=makeQuery(id+"F4.boolean.opBoolean","MERGE",EDGE,{"derivedFrom":[makeQuery(id+"F1.opExtrude","SWEPT_EDGE",EDGE,{"disambiguationData":[OSD([subQ1,subQ0])]}),makeQuery(id+"F2.opExtrude","SWEPT_EDGE",EDGE,{"disambiguationData":[OSD([subQ1,subQ0])]})]});}
            var Q6;
            Q6=makeQuery(id+"F2.opExtrude","SWEPT_EDGE",EDGE,{"disambiguationData":[OSD([sQuery(id+"F0.wireOp",EDGE,"E9.1"),sQuery(id+"F0.wireOp",EDGE,"E9.2")])]});
            var Q7;
            {var subQ0=sQuery(id+"F0.wireOp",EDGE,"E11.2");var subQ1=sQuery(id+"F0.wireOp",EDGE,"E9.1");Q7=makeQuery(id+"F2.boolean.opBoolean","MERGE",EDGE,{"derivedFrom":[makeQuery(id+"F1.opExtrude","SWEPT_EDGE",EDGE,{"disambiguationData":[OSD([subQ1,subQ0])]}),makeQuery(id+"F2.opExtrude","SWEPT_EDGE",EDGE,{"disambiguationData":[OSD([subQ1,subQ0])]})]});}
            var Q8;
            {var subQ0=sQuery(id+"F0.wireOp",EDGE,"E11.1");var subQ1=sQuery(id+"F0.wireOp",EDGE,"E9.2");Q8=makeQuery(id+"F2.boolean.opBoolean","MERGE",EDGE,{"derivedFrom":[makeQuery(id+"F1.opExtrude","SWEPT_EDGE",EDGE,{"disambiguationData":[OSD([subQ1,subQ0])]}),makeQuery(id+"F2.opExtrude","SWEPT_EDGE",EDGE,{"disambiguationData":[OSD([subQ1,subQ0])]})]});}
            var Q9;
            {var subQ0=sQuery(id+"F0.wireOp",EDGE,"E10.2");var subQ1=sQuery(id+"F0.wireOp",EDGE,"E9.1");Q9=makeQuery(id+"F2.boolean.opBoolean","MERGE",EDGE,{"derivedFrom":[makeQuery(id+"F1.opExtrude","SWEPT_EDGE",EDGE,{"disambiguationData":[OSD([subQ1,subQ0])]}),makeQuery(id+"F2.opExtrude","SWEPT_EDGE",EDGE,{"disambiguationData":[OSD([subQ1,subQ0])]})]});}
            var Q10;
            {var subQ0=sQuery(id+"F0.wireOp",EDGE,"E21");var subQ1=sQuery(id+"F0.wireOp",EDGE,"E11.1");Q10=makeQuery(id+"F2.boolean.opBoolean","MERGE",EDGE,{"derivedFrom":[makeQuery(id+"F1.opExtrude","SWEPT_EDGE",EDGE,{"disambiguationData":[OSD([subQ1,subQ0])]}),makeQuery(id+"F2.opExtrude","SWEPT_EDGE",EDGE,{"disambiguationData":[OSD([subQ1,subQ0])]})]});}
            var Q11;
            {var subQ0=sQuery(id+"F0.wireOp",EDGE,"E23");var subQ1=sQuery(id+"F0.wireOp",EDGE,"E10.2");Q11=makeQuery(id+"F2.boolean.opBoolean","MERGE",EDGE,{"derivedFrom":[makeQuery(id+"F1.opExtrude","SWEPT_EDGE",EDGE,{"disambiguationData":[OSD([subQ1,subQ0])]}),makeQuery(id+"F2.opExtrude","SWEPT_EDGE",EDGE,{"disambiguationData":[OSD([subQ1,subQ0])]})]});}
            var Q12;
            {var subQ0=sQuery(id+"F0.wireOp",EDGE,"E10.2");var subQ1=sQuery(id+"F0.wireOp",EDGE,"E9.3");Q12=makeQuery(id+"F4.boolean.opBoolean","MERGE",EDGE,{"derivedFrom":[makeQuery(id+"F1.opExtrude","SWEPT_EDGE",EDGE,{"disambiguationData":[OSD([subQ1,subQ0])]}),makeQuery(id+"F2.opExtrude","SWEPT_EDGE",EDGE,{"disambiguationData":[OSD([subQ1,subQ0])]})]});}
            var Q13;
            {var subQ0=sQuery(id+"F0.wireOp",EDGE,"E22");var subQ1=sQuery(id+"F0.wireOp",EDGE,"E10.2");Q13=makeQuery(id+"F2.boolean.opBoolean","MERGE",EDGE,{"derivedFrom":[makeQuery(id+"F1.opExtrude","SWEPT_EDGE",EDGE,{"disambiguationData":[OSD([subQ1,subQ0])]}),makeQuery(id+"F2.opExtrude","SWEPT_EDGE",EDGE,{"disambiguationData":[OSD([subQ1,subQ0])]})]});}
            var Q14;
            {var subQ0=sQuery(id+"F0.wireOp",EDGE,"E22");var subQ1=sQuery(id+"F0.wireOp",EDGE,"E11.2");Q14=makeQuery(id+"F2.boolean.opBoolean","MERGE",EDGE,{"derivedFrom":[makeQuery(id+"F1.opExtrude","SWEPT_EDGE",EDGE,{"disambiguationData":[OSD([subQ1,subQ0])]}),makeQuery(id+"F2.opExtrude","SWEPT_EDGE",EDGE,{"disambiguationData":[OSD([subQ1,subQ0])]})]});}
            var Q15;
            {var subQ0=sQuery(id+"F0.wireOp",EDGE,"E10.1");var subQ1=sQuery(id+"F0.wireOp",EDGE,"E9.2");Q15=makeQuery(id+"F2.boolean.opBoolean","MERGE",EDGE,{"derivedFrom":[makeQuery(id+"F1.opExtrude","SWEPT_EDGE",EDGE,{"disambiguationData":[OSD([subQ1,subQ0])]}),makeQuery(id+"F2.opExtrude","SWEPT_EDGE",EDGE,{"disambiguationData":[OSD([subQ1,subQ0])]})]});}
            var Q16;
            {var subQ0=sQuery(id+"F0.wireOp",EDGE,"E21");var subQ1=sQuery(id+"F0.wireOp",EDGE,"E10.1");Q16=makeQuery(id+"F2.boolean.opBoolean","MERGE",EDGE,{"derivedFrom":[makeQuery(id+"F1.opExtrude","SWEPT_EDGE",EDGE,{"disambiguationData":[OSD([subQ1,subQ0])]}),makeQuery(id+"F2.opExtrude","SWEPT_EDGE",EDGE,{"disambiguationData":[OSD([subQ1,subQ0])]})]});}
            var Q17;
            {var subQ0=sQuery(id+"F0.wireOp",EDGE,"E20");var subQ1=sQuery(id+"F0.wireOp",EDGE,"E11.1");Q17=makeQuery(id+"F2.boolean.opBoolean","MERGE",EDGE,{"derivedFrom":[makeQuery(id+"F1.opExtrude","SWEPT_EDGE",EDGE,{"disambiguationData":[OSD([subQ1,subQ0])]}),makeQuery(id+"F2.opExtrude","SWEPT_EDGE",EDGE,{"disambiguationData":[OSD([subQ1,subQ0])]})]});}
            var Q18;
            {var subQ0=sQuery(id+"F0.wireOp",EDGE,"E10.0");var subQ1=sQuery(id+"F0.wireOp",EDGE,"E9.1");Q18=makeQuery(id+"F2.boolean.opBoolean","MERGE",EDGE,{"derivedFrom":[makeQuery(id+"F1.opExtrude","SWEPT_EDGE",EDGE,{"disambiguationData":[OSD([subQ1,subQ0])]}),makeQuery(id+"F2.opExtrude","SWEPT_EDGE",EDGE,{"disambiguationData":[OSD([subQ1,subQ0])]})]});}
            var Q19;
            {var subQ0=sQuery(id+"F0.wireOp",EDGE,"E19");var subQ1=sQuery(id+"F0.wireOp",EDGE,"E10.0");Q19=makeQuery(id+"F2.boolean.opBoolean","MERGE",EDGE,{"derivedFrom":[makeQuery(id+"F1.opExtrude","SWEPT_EDGE",EDGE,{"disambiguationData":[OSD([subQ1,subQ0])]}),makeQuery(id+"F2.opExtrude","SWEPT_EDGE",EDGE,{"disambiguationData":[OSD([subQ1,subQ0])]})]});}
            var Q20;
            {var subQ0=sQuery(id+"F0.wireOp",EDGE,"E19");var subQ1=sQuery(id+"F0.wireOp",EDGE,"E11.0");Q20=makeQuery(id+"F2.boolean.opBoolean","MERGE",EDGE,{"derivedFrom":[makeQuery(id+"F1.opExtrude","SWEPT_EDGE",EDGE,{"disambiguationData":[OSD([subQ1,subQ0])]}),makeQuery(id+"F2.opExtrude","SWEPT_EDGE",EDGE,{"disambiguationData":[OSD([subQ1,subQ0])]})]});}
            var Q21;
            {var subQ0=sQuery(id+"F0.wireOp",EDGE,"E11.0");var subQ1=sQuery(id+"F0.wireOp",EDGE,"E9.1");Q21=makeQuery(id+"F2.boolean.opBoolean","MERGE",EDGE,{"derivedFrom":[makeQuery(id+"F1.opExtrude","SWEPT_EDGE",EDGE,{"disambiguationData":[OSD([subQ1,subQ0])]}),makeQuery(id+"F2.opExtrude","SWEPT_EDGE",EDGE,{"disambiguationData":[OSD([subQ1,subQ0])]})]});}
            var Q22;
            {var subQ0=sQuery(id+"F0.wireOp",EDGE,"E11.1");var subQ1=sQuery(id+"F0.wireOp",EDGE,"E9.0");Q22=makeQuery(id+"F2.boolean.opBoolean","MERGE",EDGE,{"derivedFrom":[makeQuery(id+"F1.opExtrude","SWEPT_EDGE",EDGE,{"disambiguationData":[OSD([subQ1,subQ0])]}),makeQuery(id+"F2.opExtrude","SWEPT_EDGE",EDGE,{"disambiguationData":[OSD([subQ1,subQ0])]})]});}
            var Q23;
            {var subQ0=sQuery(id+"F0.wireOp",EDGE,"E10.1");var subQ1=sQuery(id+"F0.wireOp",EDGE,"E9.0");Q23=makeQuery(id+"F2.boolean.opBoolean","MERGE",EDGE,{"derivedFrom":[makeQuery(id+"F1.opExtrude","SWEPT_EDGE",EDGE,{"disambiguationData":[OSD([subQ1,subQ0])]}),makeQuery(id+"F2.opExtrude","SWEPT_EDGE",EDGE,{"disambiguationData":[OSD([subQ1,subQ0])]})]});}
            var Q24;
            {var subQ0=sQuery(id+"F0.wireOp",EDGE,"E11.0");var subQ1=sQuery(id+"F0.wireOp",EDGE,"E9.3");Q24=makeQuery(id+"F4.boolean.opBoolean","MERGE",EDGE,{"derivedFrom":[makeQuery(id+"F1.opExtrude","SWEPT_EDGE",EDGE,{"disambiguationData":[OSD([subQ1,subQ0])]}),makeQuery(id+"F2.opExtrude","SWEPT_EDGE",EDGE,{"disambiguationData":[OSD([subQ1,subQ0])]})]});}
            var Q25;
            {var subQ0=sQuery(id+"F0.wireOp",EDGE,"E18");var subQ1=sQuery(id+"F0.wireOp",EDGE,"E11.0");Q25=makeQuery(id+"F2.boolean.opBoolean","MERGE",EDGE,{"derivedFrom":[makeQuery(id+"F1.opExtrude","SWEPT_EDGE",EDGE,{"disambiguationData":[OSD([subQ1,subQ0])]}),makeQuery(id+"F2.opExtrude","SWEPT_EDGE",EDGE,{"disambiguationData":[OSD([subQ1,subQ0])]})]});}
            var Q26;
            {var subQ0=sQuery(id+"F0.wireOp",EDGE,"E18");var subQ1=sQuery(id+"F0.wireOp",EDGE,"E10.0");Q26=makeQuery(id+"F2.boolean.opBoolean","MERGE",EDGE,{"derivedFrom":[makeQuery(id+"F1.opExtrude","SWEPT_EDGE",EDGE,{"disambiguationData":[OSD([subQ1,subQ0])]}),makeQuery(id+"F2.opExtrude","SWEPT_EDGE",EDGE,{"disambiguationData":[OSD([subQ1,subQ0])]})]});}
            var Q27;
            {var subQ0=sQuery(id+"F0.wireOp",EDGE,"E10.0");var subQ1=sQuery(id+"F0.wireOp",EDGE,"E9.3");Q27=makeQuery(id+"F4.boolean.opBoolean","MERGE",EDGE,{"derivedFrom":[makeQuery(id+"F1.opExtrude","SWEPT_EDGE",EDGE,{"disambiguationData":[OSD([subQ1,subQ0])]}),makeQuery(id+"F2.opExtrude","SWEPT_EDGE",EDGE,{"disambiguationData":[OSD([subQ1,subQ0])]})]});}
            var Q28;
            {var subQ0=sQuery(id+"F0.wireOp",EDGE,"E20");var subQ1=sQuery(id+"F0.wireOp",EDGE,"E10.1");Q28=makeQuery(id+"F2.boolean.opBoolean","MERGE",EDGE,{"derivedFrom":[makeQuery(id+"F1.opExtrude","SWEPT_EDGE",EDGE,{"disambiguationData":[OSD([subQ1,subQ0])]}),makeQuery(id+"F2.opExtrude","SWEPT_EDGE",EDGE,{"disambiguationData":[OSD([subQ1,subQ0])]})]});}
            var Q29;
            Q29=makeQuery(id+"F2.opExtrude","SWEPT_EDGE",EDGE,{"disambiguationData":[OSD([sQuery(id+"F0.wireOp",EDGE,"E9.0"),sQuery(id+"F0.wireOp",EDGE,"E9.1")])]});
            var Q30;
            Q30=makeQuery(id+"F2.opExtrude","SWEPT_EDGE",EDGE,{"disambiguationData":[OSD([sQuery(id+"F0.wireOp",EDGE,"E9.0"),sQuery(id+"F0.wireOp",EDGE,"E9.3")])]});
            var Q31;
            {var subQ0=sQuery(id+"F0.wireOp",EDGE,"E12.2");var subQ1=sQuery(id+"F0.wireOp",EDGE,"E10.1");Q31=makeQuery(id+"F2.boolean.opBoolean","MERGE",EDGE,{"derivedFrom":[makeQuery(id+"F1.opExtrude","SWEPT_EDGE",EDGE,{"disambiguationData":[OSD([subQ1,subQ0])]}),makeQuery(id+"F2.opExtrude","SWEPT_EDGE",EDGE,{"disambiguationData":[OSD([subQ1,subQ0])]})]});}
            var Q32;
            {var subQ0=sQuery(id+"F0.wireOp",EDGE,"E12.1");var subQ1=sQuery(id+"F0.wireOp",EDGE,"E10.2");Q32=makeQuery(id+"F2.boolean.opBoolean","MERGE",EDGE,{"derivedFrom":[makeQuery(id+"F1.opExtrude","SWEPT_EDGE",EDGE,{"disambiguationData":[OSD([subQ1,subQ0])]}),makeQuery(id+"F2.opExtrude","SWEPT_EDGE",EDGE,{"disambiguationData":[OSD([subQ1,subQ0])]})]});}
            var Q33;
            {var subQ0=sQuery(id+"F0.wireOp",EDGE,"E10.2");var subQ1=sQuery(id+"F0.wireOp",EDGE,"E10.1");Q33=makeQuery(id+"F2.boolean.opBoolean","MERGE",EDGE,{"derivedFrom":[makeQuery(id+"F1.opExtrude","SWEPT_EDGE",EDGE,{"disambiguationData":[OSD([subQ1,subQ0])]}),makeQuery(id+"F2.opExtrude","SWEPT_EDGE",EDGE,{"disambiguationData":[OSD([subQ1,subQ0])]})]});}
            var Q34;
            {var subQ0=sQuery(id+"F0.wireOp",EDGE,"E12.2");var subQ1=sQuery(id+"F0.wireOp",EDGE,"E9.3");Q34=makeQuery(id+"F4.boolean.opBoolean","MERGE",EDGE,{"derivedFrom":[makeQuery(id+"F1.opExtrude","SWEPT_EDGE",EDGE,{"disambiguationData":[OSD([subQ1,subQ0])]}),makeQuery(id+"F2.opExtrude","SWEPT_EDGE",EDGE,{"disambiguationData":[OSD([subQ1,subQ0])]})]});}
            var Q35;
            {var subQ0=sQuery(id+"F0.wireOp",EDGE,"E12.1");var subQ1=sQuery(id+"F0.wireOp",EDGE,"E10.0");Q35=makeQuery(id+"F2.boolean.opBoolean","MERGE",EDGE,{"derivedFrom":[makeQuery(id+"F1.opExtrude","SWEPT_EDGE",EDGE,{"disambiguationData":[OSD([subQ1,subQ0])]}),makeQuery(id+"F2.opExtrude","SWEPT_EDGE",EDGE,{"disambiguationData":[OSD([subQ1,subQ0])]})]});}
            var Q36;
            {var subQ0=sQuery(id+"F0.wireOp",EDGE,"E10.1");var subQ1=sQuery(id+"F0.wireOp",EDGE,"E10.0");Q36=makeQuery(id+"F2.boolean.opBoolean","MERGE",EDGE,{"derivedFrom":[makeQuery(id+"F1.opExtrude","SWEPT_EDGE",EDGE,{"disambiguationData":[OSD([subQ1,subQ0])]}),makeQuery(id+"F2.opExtrude","SWEPT_EDGE",EDGE,{"disambiguationData":[OSD([subQ1,subQ0])]})]});}
            var Q37;
            {var subQ0=sQuery(id+"F0.wireOp",EDGE,"E12.0");var subQ1=sQuery(id+"F0.wireOp",EDGE,"E10.1");Q37=makeQuery(id+"F2.boolean.opBoolean","MERGE",EDGE,{"derivedFrom":[makeQuery(id+"F1.opExtrude","SWEPT_EDGE",EDGE,{"disambiguationData":[OSD([subQ1,subQ0])]}),makeQuery(id+"F2.opExtrude","SWEPT_EDGE",EDGE,{"disambiguationData":[OSD([subQ1,subQ0])]})]});}
            var Q38;
            {var subQ0=sQuery(id+"F0.wireOp",EDGE,"E12.0");var subQ1=sQuery(id+"F0.wireOp",EDGE,"E9.3");Q38=makeQuery(id+"F4.boolean.opBoolean","MERGE",EDGE,{"derivedFrom":[makeQuery(id+"F1.opExtrude","SWEPT_EDGE",EDGE,{"disambiguationData":[OSD([subQ1,subQ0])]}),makeQuery(id+"F2.opExtrude","SWEPT_EDGE",EDGE,{"disambiguationData":[OSD([subQ1,subQ0])]})]});}
            var Q39;
            {var subQ0=sQuery(id+"F0.wireOp",EDGE,"E23");var subQ1=sQuery(id+"F0.wireOp",EDGE,"E11.2");Q39=makeQuery(id+"F2.boolean.opBoolean","MERGE",EDGE,{"derivedFrom":[makeQuery(id+"F1.opExtrude","SWEPT_EDGE",EDGE,{"disambiguationData":[OSD([subQ1,subQ0])]}),makeQuery(id+"F2.opExtrude","SWEPT_EDGE",EDGE,{"disambiguationData":[OSD([subQ1,subQ0])]})]});}
            chamfer(context, id + "F9", {"entities" : qUnion([Q0, Q1, Q2, Q3, Q4, Q5, Q6, Q7, Q8, Q9, Q10, Q11, Q12, Q13, Q14, Q15, Q16, Q17, Q18, Q19, Q20, Q21, Q22, Q23, Q24, Q25, Q26, Q27, Q28, Q29, Q30, Q31, Q32, Q33, Q34, Q35, Q36, Q37, Q38, Q39]), "width" : 2 * mm});
        }
        {
            var Q0;
            {var subQ0=sQuery(id+"F0.wireOp",EDGE,"E14");Q0=makeQuery(id+"F7.boolean.opBoolean","MERGE",FACE,{"derivedFrom":[makeQuery(id+"F4.boolean.opBoolean","MERGE",FACE,{"derivedFrom":[makeQuery(id+"F1.opExtrude","SWEPT_FACE",FACE,{"disambiguationData":[OSD([subQ0])]}),makeQuery(id+"F4.opExtrude","SWEPT_FACE",FACE,{"disambiguationData":[OSD([subQ0])]})]}),makeQuery(id+"F7.opExtrude","SWEPT_FACE",FACE,{"disambiguationData":[OSD([sQuery(id+"F5.wireOp",EDGE,"E28.left")])]})]});}
            var sketch = newSketch(context, id + "F10", { "sketchPlane" : qUnion([Q0])});
            skLineSegment(sketch, "E51", {"start": v(44.5, 16) * mm, "end": v(44.7, 16.2) * mm});
            skLineSegment(sketch, "E52", {"start": v(44.7, 16.2) * mm, "end": v(46.7, 16.2) * mm});
            skLineSegment(sketch, "E53", {"start": v(46.7, 16.2) * mm, "end": v(46.9, 16) * mm});
            skLineSegment(sketch, "E54", {"start": v(46.9, 16) * mm, "end": v(44.5, 16) * mm});
            skPoint(sketch, "E55", {"position": v(45.7, 16) * mm});
            skLineSegment(sketch, "E56.bottom", {"start": v(43.2, 15.4) * mm, "end": v(48.2, 15.4) * mm});
            skLineSegment(sketch, "E56.top", {"start": v(43.2, 14.4) * mm, "end": v(48.2, 14.4) * mm});
            skLineSegment(sketch, "E56.left", {"start": v(43.2, 15.4) * mm, "end": v(43.2, 14.4) * mm});
            skLineSegment(sketch, "E56.right", {"start": v(48.2, 15.4) * mm, "end": v(48.2, 14.4) * mm});
            skPoint(sketch, "E57", {"position": v(45.7, 15.4) * mm});
            skSolve(sketch);
        }
        {
            var Q0;
            Q0=makeQuery(id+"F10.imprint","IMPRINT",FACE,{"disambiguationData":[TD([[makeQuery(id+"F10.imprint","IMPRINT",EDGE,{"derivedFrom":sQuery(id+"F10.wireOp",EDGE,"E51")}),-1.0]])]});
            var Q1;
            {var subQ0=sQuery(id+"F0.wireOp",EDGE,"E16");Q1=makeQuery(id+"F7.boolean.opBoolean","MERGE",FACE,{"derivedFrom":[makeQuery(id+"F4.boolean.opBoolean","MERGE",FACE,{"derivedFrom":[makeQuery(id+"F1.opExtrude","SWEPT_FACE",FACE,{"disambiguationData":[OSD([subQ0])]}),makeQuery(id+"F4.opExtrude","SWEPT_FACE",FACE,{"disambiguationData":[OSD([subQ0])]})]}),makeQuery(id+"F7.opExtrude","SWEPT_FACE",FACE,{"disambiguationData":[OSD([sQuery(id+"F5.wireOp",EDGE,"E28.right")])]})]});}
            extrude(context, id + "F11", {"entities" : qUnion([Q0]), "operationType" : NewBodyOperationType.ADD, "endBound" : BoundingType.UP_TO_SURFACE, "oppositeDirection" : true, "depth" : 25 * mm, "endBoundEntityFace" : qUnion([Q1]), "offsetDistance" : 25 * mm});
        }
        {
            var Q0;
            {var subQ5=sQuery(id+"F5.wireOp",EDGE,"E34.4");Q0=makeQuery(id+"F5.imprint","IMPRINT",FACE,{"disambiguationData":[TD([[makeQuery(id+"F5.imprint","IMPRINT",EDGE,{"derivedFrom":subQ5}),-1.0]])]});}
            var Q1;
            {var subQ5=sQuery(id+"F5.wireOp",EDGE,"E35.4");Q1=makeQuery(id+"F5.imprint","IMPRINT",FACE,{"disambiguationData":[TD([[makeQuery(id+"F5.imprint","IMPRINT",EDGE,{"derivedFrom":subQ5}),-1.0]])]});}
            var Q2;
            {var subQ5=sQuery(id+"F5.wireOp",EDGE,"E36.4");Q2=makeQuery(id+"F5.imprint","IMPRINT",FACE,{"disambiguationData":[TD([[makeQuery(id+"F5.imprint","IMPRINT",EDGE,{"derivedFrom":subQ5}),-1.0]])]});}
            var Q3;
            {var subQ5=sQuery(id+"F5.wireOp",EDGE,"E37.4");Q3=makeQuery(id+"F5.imprint","IMPRINT",FACE,{"disambiguationData":[TD([[makeQuery(id+"F5.imprint","IMPRINT",EDGE,{"derivedFrom":subQ5}),-1.0]])]});}
            extrude(context, id + "F12", {"entities" : qUnion([Q0, Q1, Q2, Q3]), "operationType" : NewBodyOperationType.REMOVE, "endBound" : BoundingType.THROUGH_ALL, "depth" : 25 * mm, "offsetDistance" : 25 * mm});
        }
        {
            var Q0;
            Q0=makeQuery(id+"F10.imprint","IMPRINT",FACE,{"disambiguationData":[TD([[makeQuery(id+"F10.imprint","IMPRINT",EDGE,{"derivedFrom":sQuery(id+"F10.wireOp",EDGE,"E56.bottom")}),-1.0]])]});
            extrude(context, id + "F13", {"entities" : qUnion([Q0]), "operationType" : NewBodyOperationType.REMOVE, "endBound" : BoundingType.THROUGH_ALL, "oppositeDirection" : true, "depth" : 25 * mm, "offsetDistance" : 25 * mm});
        }
        {
            var Q0;
            Q0=makeQuery(id+"F1.opExtrude","CAP_FACE",FACE,{"disambiguationData":[OSD([sQuery(id+"F0.wireOp",EDGE,"E1"),sQuery(id+"F0.wireOp",EDGE,"E2"),sQuery(id+"F0.wireOp",EDGE,"E3"),sQuery(id+"F0.wireOp",EDGE,"E4"),sQuery(id+"F0.wireOp",EDGE,"E9.0"),sQuery(id+"F0.wireOp",EDGE,"E9.1"),sQuery(id+"F0.wireOp",EDGE,"E9.2"),sQuery(id+"F0.wireOp",EDGE,"E9.3"),sQuery(id+"F0.wireOp",EDGE,"E10.0"),sQuery(id+"F0.wireOp",EDGE,"E10.1"),sQuery(id+"F0.wireOp",EDGE,"E10.2"),sQuery(id+"F0.wireOp",EDGE,"E11.0"),sQuery(id+"F0.wireOp",EDGE,"E11.1"),sQuery(id+"F0.wireOp",EDGE,"E11.2"),sQuery(id+"F0.wireOp",EDGE,"E12.0"),sQuery(id+"F0.wireOp",EDGE,"E12.1"),sQuery(id+"F0.wireOp",EDGE,"E12.2"),sQuery(id+"F0.wireOp",EDGE,"E13.0"),sQuery(id+"F0.wireOp",EDGE,"E13.1"),sQuery(id+"F0.wireOp",EDGE,"E13.2"),sQuery(id+"F0.wireOp",EDGE,"E13.3"),sQuery(id+"F0.wireOp",EDGE,"E14"),sQuery(id+"F0.wireOp",EDGE,"E15"),sQuery(id+"F0.wireOp",EDGE,"E16"),sQuery(id+"F0.wireOp",EDGE,"E18"),sQuery(id+"F0.wireOp",EDGE,"E19"),sQuery(id+"F0.wireOp",EDGE,"E20"),sQuery(id+"F0.wireOp",EDGE,"E21"),sQuery(id+"F0.wireOp",EDGE,"E22"),sQuery(id+"F0.wireOp",EDGE,"E23")])],"isStart":false});
            var sketch = newSketch(context, id + "F14", { "sketchPlane" : qUnion([Q0])});
            skLineSegment(sketch, "E58.bottom", {"start": v(-83.5, 44.5) * mm, "end": v(-50.44, 44.5) * mm});
            skLineSegment(sketch, "E58.top", {"start": v(-83.5, 48.5) * mm, "end": v(-50.44, 48.5) * mm});
            skLineSegment(sketch, "E58.left", {"start": v(-83.5, 44.5) * mm, "end": v(-83.5, 48.5) * mm});
            skLineSegment(sketch, "E59.right", {"start": v(-50.44, 44.5) * mm, "end": v(-50.44, 48.5) * mm});
            skLineSegment(sketch, "E60.bottom", {"start": v(-35.06, 44.5) * mm, "end": v(-21.94, 44.5) * mm});
            skLineSegment(sketch, "E60.top", {"start": v(-35.06, 48.5) * mm, "end": v(-21.94, 48.5) * mm});
            skLineSegment(sketch, "E60.left", {"start": v(-35.06, 44.5) * mm, "end": v(-35.06, 48.5) * mm});
            skLineSegment(sketch, "E60.right", {"start": v(-21.94, 44.5) * mm, "end": v(-21.94, 48.5) * mm});
            skLineSegment(sketch, "E61.bottom", {"start": v(-6.56, 44.5) * mm, "end": v(6.56, 44.5) * mm});
            skLineSegment(sketch, "E61.top", {"start": v(-6.56, 48.5) * mm, "end": v(6.56, 48.5) * mm});
            skLineSegment(sketch, "E61.left", {"start": v(-6.56, 44.5) * mm, "end": v(-6.56, 48.5) * mm});
            skLineSegment(sketch, "E61.right", {"start": v(6.56, 44.5) * mm, "end": v(6.56, 48.5) * mm});
            skLineSegment(sketch, "E62.bottom", {"start": v(21.94, 44.5) * mm, "end": v(35.06, 44.5) * mm});
            skLineSegment(sketch, "E62.top", {"start": v(21.94, 48.5) * mm, "end": v(35.06, 48.5) * mm});
            skLineSegment(sketch, "E62.left", {"start": v(21.94, 44.5) * mm, "end": v(21.94, 48.5) * mm});
            skLineSegment(sketch, "E62.right", {"start": v(35.06, 44.5) * mm, "end": v(35.06, 48.5) * mm});
            skLineSegment(sketch, "E63.left", {"start": v(50.44, 44.5) * mm, "end": v(50.44, 48.5) * mm});
            skLineSegment(sketch, "E64.bottom", {"start": v(50.44, 44.5) * mm, "end": v(83.5, 44.5) * mm});
            skLineSegment(sketch, "E64.top", {"start": v(50.44, 48.5) * mm, "end": v(83.5, 48.5) * mm});
            skLineSegment(sketch, "E64.right", {"start": v(83.5, 44.5) * mm, "end": v(83.5, 48.5) * mm});
            skLineSegment(sketch, "E65", {"start": v(-50.44, 48.5) * mm, "end": v(50.44, 48.5) * mm});
            skLineSegment(sketch, "E66", {"start": v(50.44, 44.5) * mm, "end": v(-50.44, 44.5) * mm});
            skSolve(sketch);
        }
        {
            var Q0;
            Q0=makeQuery(id+"F14.imprint","IMPRINT",FACE,{"disambiguationData":[TD([[makeQuery(id+"F14.imprint","IMPRINT",EDGE,{"derivedFrom":sQuery(id+"F14.wireOp",EDGE,"E58.bottom")}),1.0]])]});
            var Q1;
            {var subQ0=sQuery(id+"F14.wireOp",EDGE,"E59.right");Q1=makeQuery(id+"F14.imprint","IMPRINT",FACE,{"disambiguationData":[TD([[makeQuery(id+"F14.imprint","IMPRINT",EDGE,{"derivedFrom":subQ0}),-1.0]])]});}
            var Q2;
            {var subQ0=sQuery(id+"F14.wireOp",EDGE,"E60.left");Q2=makeQuery(id+"F14.imprint","IMPRINT",FACE,{"disambiguationData":[TD([[makeQuery(id+"F14.imprint","IMPRINT",EDGE,{"derivedFrom":subQ0}),-1.0]])]});}
            var Q3;
            {var subQ0=sQuery(id+"F14.wireOp",EDGE,"E60.right");Q3=makeQuery(id+"F14.imprint","IMPRINT",FACE,{"disambiguationData":[TD([[makeQuery(id+"F14.imprint","IMPRINT",EDGE,{"derivedFrom":subQ0}),-1.0]])]});}
            var Q4;
            {var subQ0=sQuery(id+"F14.wireOp",EDGE,"E61.left");Q4=makeQuery(id+"F14.imprint","IMPRINT",FACE,{"disambiguationData":[TD([[makeQuery(id+"F14.imprint","IMPRINT",EDGE,{"derivedFrom":subQ0}),-1.0]])]});}
            var Q5;
            {var subQ0=sQuery(id+"F14.wireOp",EDGE,"E61.right");Q5=makeQuery(id+"F14.imprint","IMPRINT",FACE,{"disambiguationData":[TD([[makeQuery(id+"F14.imprint","IMPRINT",EDGE,{"derivedFrom":subQ0}),-1.0]])]});}
            var Q6;
            {var subQ0=sQuery(id+"F14.wireOp",EDGE,"E62.left");Q6=makeQuery(id+"F14.imprint","IMPRINT",FACE,{"disambiguationData":[TD([[makeQuery(id+"F14.imprint","IMPRINT",EDGE,{"derivedFrom":subQ0}),-1.0]])]});}
            var Q7;
            {var subQ0=sQuery(id+"F14.wireOp",EDGE,"E62.right");Q7=makeQuery(id+"F14.imprint","IMPRINT",FACE,{"disambiguationData":[TD([[makeQuery(id+"F14.imprint","IMPRINT",EDGE,{"derivedFrom":subQ0}),-1.0]])]});}
            var Q8;
            Q8=makeQuery(id+"F14.imprint","IMPRINT",FACE,{"disambiguationData":[TD([[makeQuery(id+"F14.imprint","IMPRINT",EDGE,{"derivedFrom":sQuery(id+"F14.wireOp",EDGE,"E63.left")}),-1.0]])]});
            extrude(context, id + "F15", {"entities" : qUnion([Q0, Q1, Q2, Q3, Q4, Q5, Q6, Q7, Q8]), "oppositeDirection" : true, "depth" : .4 * mm, "offsetDistance" : 25 * mm});
        }
        {
            var Q0;
            Q0=makeQuery(id+"F14.imprint","IMPRINT",FACE,{"disambiguationData":[TD([[makeQuery(id+"F14.imprint","IMPRINT",EDGE,{"derivedFrom":sQuery(id+"F14.wireOp",EDGE,"E58.bottom")}),1.0]])]});
            var Q1;
            Q1=makeQuery(id+"F14.imprint","IMPRINT",FACE,{"disambiguationData":[TD([[makeQuery(id+"F14.imprint","IMPRINT",EDGE,{"derivedFrom":sQuery(id+"F14.wireOp",EDGE,"E64.bottom")}),1.0]])]});
            var Q2;
            {var subQ0=sQuery(id+"F14.wireOp",EDGE,"E60.left");Q2=makeQuery(id+"F14.imprint","IMPRINT",FACE,{"disambiguationData":[TD([[makeQuery(id+"F14.imprint","IMPRINT",EDGE,{"derivedFrom":subQ0}),-1.0]])]});}
            var Q3;
            {var subQ0=sQuery(id+"F14.wireOp",EDGE,"E61.left");Q3=makeQuery(id+"F14.imprint","IMPRINT",FACE,{"disambiguationData":[TD([[makeQuery(id+"F14.imprint","IMPRINT",EDGE,{"derivedFrom":subQ0}),-1.0]])]});}
            var Q4;
            {var subQ0=sQuery(id+"F14.wireOp",EDGE,"E62.left");Q4=makeQuery(id+"F14.imprint","IMPRINT",FACE,{"disambiguationData":[TD([[makeQuery(id+"F14.imprint","IMPRINT",EDGE,{"derivedFrom":subQ0}),-1.0]])]});}
            var Q5;
            {var subQ0=sQuery(id+"F5.wireOp",EDGE,"E28.top");var subQ1=makeQuery(id+"F5.imprint","INTERSECT",VERTEX,{"derivedFrom":[subQ0,sQuery(id+"F5.wireOp",EDGE,"E46")]});var subQ2=sQuery(id+"F5.wireOp",EDGE,"E31");var subQ4=makeQuery(id+"F5.imprint","INTERSECT",VERTEX,{"disambiguationData":[OD(0.0)],"derivedFrom":[subQ0,subQ2]});var subQ5=makeQuery(id+"F5.imprint","INTERSECT",VERTEX,{"derivedFrom":[subQ0,sQuery(id+"F5.wireOp",EDGE,"E45")]});Q5=makeQuery(id+"F8.opChamfer","SPLIT",FACE,{"disambiguationData":[OD(0.0)],"derivedFrom":makeQuery(id+"FDtMRLwZ7YmErVr_1.boolean.opBoolean","MERGE",FACE,{"derivedFrom":[makeQuery(id+"F7.opExtrude","SWEPT_FACE",FACE,{"disambiguationData":[OSD([subQ0]),TDD([makeQuery(id+"F5.imprint","IMPRINT",EDGE,{"disambiguationData":[TD([[subQ5,1.0]])],"derivedFrom":subQ0})])]}),makeQuery(id+"F7.opExtrude","SWEPT_FACE",FACE,{"disambiguationData":[OSD([subQ0]),TDD([makeQuery(id+"F5.imprint","IMPRINT",EDGE,{"disambiguationData":[TD([[subQ1,-1.0]])],"derivedFrom":subQ0})])]}),makeQuery(id+"FDtMRLwZ7YmErVr_1.opExtrude","SWEPT_FACE",FACE,{"disambiguationData":[OSD([subQ0]),TDD([makeQuery(id+"F5.imprint","IMPRINT",EDGE,{"disambiguationData":[TD([[subQ5,-1.0]])],"derivedFrom":subQ0}),makeQuery(id+"F5.imprint","IMPRINT",EDGE,{"disambiguationData":[TD([[subQ4,-1.0]])],"derivedFrom":subQ0}),makeQuery(id+"F5.imprint","IMPRINT",EDGE,{"disambiguationData":[TD([[subQ1,1.0]])],"derivedFrom":subQ0})])]})]})});}
            extrude(context, id + "F16", {"entities" : qUnion([Q0, Q1, Q2, Q3, Q4]), "operationType" : NewBodyOperationType.ADD, "endBound" : BoundingType.UP_TO_SURFACE, "oppositeDirection" : true, "depth" : 25 * mm, "endBoundEntityFace" : qUnion([Q5]), "hasOffset" : true, "offsetDistance" : 0.2 * mm});
        }
    });
